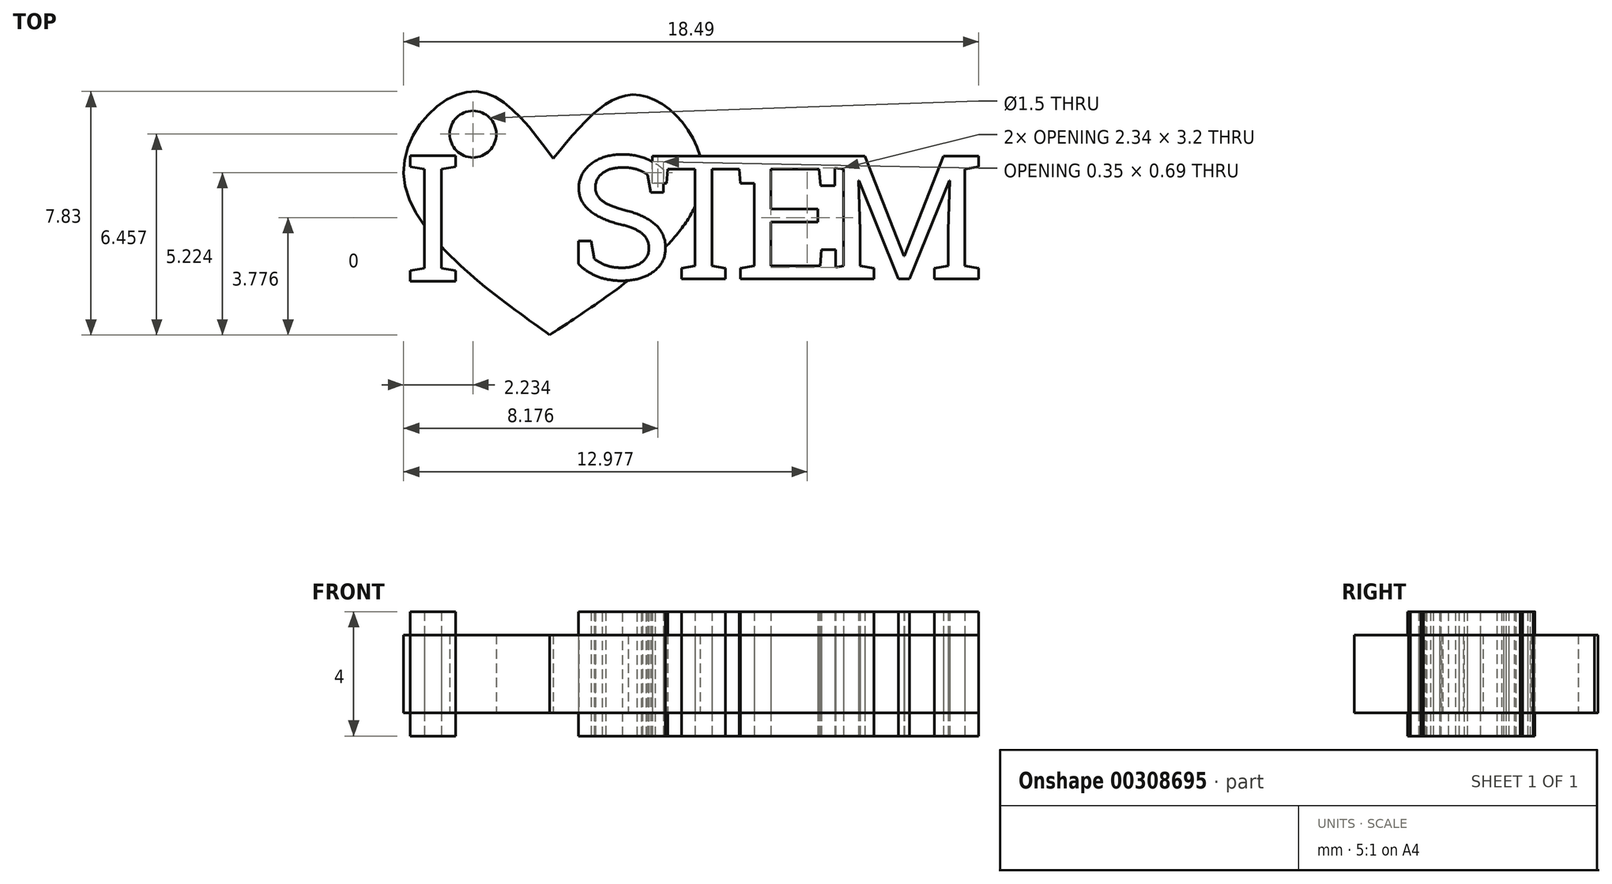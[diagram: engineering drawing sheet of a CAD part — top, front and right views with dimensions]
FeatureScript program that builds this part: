
annotation { "Feature Type Name" : "Feature", "Feature Type Description" : "" }
export const myFeature = defineFeature(function(context is Context, id is Id, definition is map)
    precondition{}
    {
        {
            var Q0;
            Q0=qCreatedBy(makeId("Top.planeOp"),FACE);
            var sketch = newSketch(context, id + "F0", { "sketchPlane" : qUnion([Q0])});
            skFitSpline(sketch, "E0", {"points": [v(-11.06, 1.77) * mm, v(-13.75, 3.93) * mm, v(-15.86, 1.08) * mm, v(-11.18, -3.9) * mm], "startDerivative": vector(-8.75, 11.76) * mm, "endDerivative": vector(10.36, -7.45) * mm});
            skLineSegment(sketch, "E1", {"start": v(-11.06, 1.77) * mm, "end": v(-11.18, -3.9) * mm});
            skFitSpline(sketch, "E2.MirrorCS", {"points": [v(-11.06, 1.77) * mm, v(-8.3, 3.82) * mm, v(-6.3, 0.88) * mm, v(-11.18, -3.9) * mm], "startDerivative": vector(9.22, 11.4) * mm, "endDerivative": vector(-10.65, -7.02) * mm});
            skCircle(sketch, "E3", {"center": v(-13.65, 2.56) * mm, "radius": 0.75 * mm});
            skText(sketch, "E4", { "text": "S", "fontName": "RobotoSlab-Regular.ttf"});
            skText(sketch, "E5", { "text": "T", "fontName": "RobotoSlab-Regular.ttf"});
            skText(sketch, "E6", { "text": "E", "fontName": "RobotoSlab-Regular.ttf"});
            skText(sketch, "E7", { "text": "M", "fontName": "RobotoSlab-Regular.ttf"});
            skText(sketch, "E8", { "text": "I", "fontName": "RobotoSlab-Regular.ttf"});
            const initialGuessF0  = {"E4": [-0.01058, -0.0021, 1, 0, 0.004], "E5": [-0.00798, -0.0021, 1, 0, 0.004], "E6": [-0.00524, -0.0021, 1, 0, 0.004], "E7": [-0.00237, -0.0021, 1, 0, 0.004], "E8": [-0.01586, -0.00218, 1, 0, 0.0041]};
            skSetInitialGuess(sketch, initialGuessF0);
            skSolve(sketch);
        }
        {
            var Q0;
            Q0 = qSketchRegion(id + "F0", true);
            extrude(context, id + "F1", {"entities" : qUnion([Q0]), "endBound" : BoundingType.SYMMETRIC, "depth" : 2.5 * mm});
        }
        {
            var Q0;
            Q0=makeQuery(id+"F0.imprint","IMPRINT",FACE,{"disambiguationData":[TD([[makeQuery(id+"F0.imprint","IMPRINT",EDGE,{"derivedFrom":sQuery(id+"F0.wireOp",EDGE,"E8.sketch_text.stroke-0")}),-1.0]])]});
            var Q1;
            {var subQ7=sQuery(id+"F0.wireOp",EDGE,"E4.sketch_text.stroke-0");Q1=makeQuery(id+"F0.imprint","IMPRINT",FACE,{"disambiguationData":[TD([[makeQuery(id+"F0.imprint","IMPRINT",EDGE,{"derivedFrom":subQ7}),-1.0]])]});}
            var Q2;
            {var subQ0=sQuery(id+"F0.wireOp",EDGE,"E4.sketch_text.stroke-29");var subQ1=sQuery(id+"F0.wireOp",EDGE,"E4.sketch_text.stroke-28");var subQ2=makeQuery(id+"F0.imprint","INTERSECT",VERTEX,{"derivedFrom":[subQ1,subQ0]});Q2=makeQuery(id+"F0.imprint","IMPRINT",FACE,{"disambiguationData":[TD([[makeQuery(id+"F0.imprint","IMPRINT",EDGE,{"disambiguationData":[TD([[subQ2,1.0]])],"derivedFrom":subQ1}),-1.0]])]});}
            var Q3;
            {var subQ5=sQuery(id+"F0.wireOp",EDGE,"E5.sketch_text.stroke-11");Q3=makeQuery(id+"F0.imprint","IMPRINT",FACE,{"disambiguationData":[TD([[makeQuery(id+"F0.imprint","IMPRINT",EDGE,{"derivedFrom":subQ5}),-1.0]])]});}
            var Q4;
            {var subQ0=sQuery(id+"F0.wireOp",EDGE,"E8.sketch_text.stroke-5");Q4=makeQuery(id+"F0.imprint","IMPRINT",FACE,{"disambiguationData":[TD([[makeQuery(id+"F0.imprint","IMPRINT",EDGE,{"derivedFrom":subQ0}),-1.0]])]});}
            var Q5;
            {var subQ5=sQuery(id+"F0.wireOp",EDGE,"E4.sketch_text.stroke-10");Q5=makeQuery(id+"F0.imprint","IMPRINT",FACE,{"disambiguationData":[TD([[makeQuery(id+"F0.imprint","IMPRINT",EDGE,{"derivedFrom":subQ5}),-1.0]])]});}
            var Q6;
            {var subQ6=sQuery(id+"F0.wireOp",EDGE,"E5.sketch_text.stroke-2");Q6=makeQuery(id+"F0.imprint","IMPRINT",FACE,{"disambiguationData":[TD([[makeQuery(id+"F0.imprint","IMPRINT",EDGE,{"derivedFrom":subQ6}),-1.0]])]});}
            var Q7;
            {var subQ4=sQuery(id+"F0.wireOp",EDGE,"E5.sketch_text.stroke-0");Q7=makeQuery(id+"F0.imprint","IMPRINT",FACE,{"disambiguationData":[TD([[makeQuery(id+"F0.imprint","IMPRINT",EDGE,{"derivedFrom":subQ4}),-1.0]])]});}
            var Q8;
            {var subQ7=sQuery(id+"F0.wireOp",EDGE,"E5.sketch_text.stroke-0");Q8=makeQuery(id+"F0.imprint","IMPRINT",FACE,{"disambiguationData":[TD([[makeQuery(id+"F0.imprint","IMPRINT",EDGE,{"derivedFrom":subQ7}),1.0]])]});}
            var Q9;
            Q9=makeQuery(id+"F0.imprint","IMPRINT",FACE,{"disambiguationData":[TD([[makeQuery(id+"F0.imprint","IMPRINT",EDGE,{"derivedFrom":sQuery(id+"F0.wireOp",EDGE,"E7.sketch_text.stroke-0")}),-1.0]])]});
            var Q10;
            {var subQ5=sQuery(id+"F0.wireOp",EDGE,"E7.sketch_text.stroke-14");Q10=makeQuery(id+"F0.imprint","IMPRINT",FACE,{"disambiguationData":[TD([[makeQuery(id+"F0.imprint","IMPRINT",EDGE,{"derivedFrom":subQ5}),-1.0]])]});}
            var Q11;
            {var subQ5=sQuery(id+"F0.wireOp",EDGE,"E7.sketch_text.stroke-10");Q11=makeQuery(id+"F0.imprint","IMPRINT",FACE,{"disambiguationData":[TD([[makeQuery(id+"F0.imprint","IMPRINT",EDGE,{"derivedFrom":subQ5}),-1.0]])]});}
            extrude(context, id + "F2", {"entities" : qUnion([Q0, Q1, Q2, Q3, Q4, Q5, Q6, Q7, Q8, Q9, Q10, Q11]), "endBound" : BoundingType.SYMMETRIC, "depth" : 4 * mm});
        }
    });
